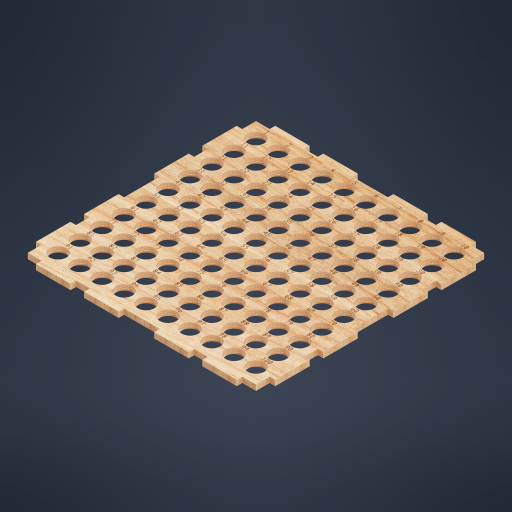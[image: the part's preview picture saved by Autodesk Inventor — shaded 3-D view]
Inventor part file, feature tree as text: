
AUTODESK INVENTOR PART (.ipt)
format: ipt  version: 2024.1 (Build 281209000, 209)  size: 6,590,464 bytes
history: native  units: mm
features: extrude x2, sketch x2, projected_geometry x1
ambient origin geometry x8: Origin, YZ Plane, XZ Plane, XY Plane, X Axis, Y Axis, Z Axis, Center Point
bodies: Solid1 (feature_tree)
feature tree (5):
  extrude  "Extrusion1"  Depth=100.0mm
  extrude  "Extrusion2"  Depth=5.0mm
  sketch  "Sketch1"  dims[d0=12.0mm d1=100.0mm d3=16.0mm]
  sketch  "Sketch2"  dims[d4=100.0mm d6=16.0mm d9=5.0mm d10=5.0mm d11=4.0mm d12=4.0mm d13=10.0mm d14=10.0mm d15=25.0mm d16=4.0mm d17=25.0mm d18=10.0mm d19=25.0mm d20=10.0mm d21=25.0mm d22=4.0mm d23=40.0mm d25=360.0deg d27=4.0mm d28=0.0mm d29=3.0mm d30=0.5mm d31=16.0mm d32=4.0mm d33=3.0mm d34=4.0mm d35=3.0mm d36=4.0mm d37=3.0mm d38=4.0mm d39=3.0mm d40=4.0mm d41=3.0mm d42=4.0mm d43=3.0mm d44=4.0mm d45=3.0mm d46=4.0mm d47=3.0mm d48=4.0mm d49=3.0mm d50=4.0mm d51=3.0mm d52=4.0mm d53=3.0mm d54=4.0mm d55=3.0mm d56=4.0mm d57=3.0mm d58=4.0mm d59=3.0mm d60=4.0mm d61=3.0mm d62=4.0mm d63=3.0mm d64=4.0mm d65=3.0mm d66=4.0mm d67=3.0mm d68=4.0mm d69=3.0mm d70=4.0mm d71=3.0mm d72=4.0mm d73=3.0mm d74=4.0mm d75=3.0mm d76=4.0mm d77=3.0mm d78=4.0mm d79=3.0mm d80=4.0mm d81=3.0mm d82=4.0mm d83=3.0mm d84=4.0mm d85=3.0mm d86=4.0mm d87=3.0mm d88=4.0mm d89=3.0mm d90=4.0mm d91=3.0mm d92=4.0mm d93=3.0mm d94=4.0mm d95=3.0mm d96=4.0mm d97=3.0mm d98=4.0mm d99=3.0mm d100=4.0mm d101=3.0mm d102=4.0mm d103=3.0mm d104=4.0mm d105=3.0mm d106=4.0mm d107=3.0mm d108=4.0mm d109=3.0mm d110=4.0mm d111=3.0mm d112=4.0mm d113=3.0mm d114=4.0mm d115=3.0mm d116=4.0mm d117=3.0mm d118=4.0mm d119=3.0mm d120=4.0mm d121=3.0mm d122=4.0mm d123=3.0mm d124=4.0mm d125=3.0mm d126=4.0mm d127=3.0mm d128=4.0mm d129=3.0mm d130=4.0mm d131=3.0mm d132=4.0mm d133=3.0mm d134=4.0mm d135=3.0mm d136=4.0mm d137=3.0mm d138=4.0mm d139=3.0mm d140=4.0mm d141=3.0mm d142=4.0mm d143=3.0mm d144=4.0mm d145=3.0mm d146=4.0mm d147=3.0mm d148=4.0mm d149=3.0mm d150=4.0mm d151=3.0mm d152=4.0mm d153=3.0mm d154=4.0mm d155=3.0mm d156=4.0mm d157=3.0mm d158=4.0mm d159=3.0mm d160=4.0mm d161=3.0mm d162=4.0mm d163=3.0mm d164=4.0mm d165=3.0mm d166=4.0mm d167=3.0mm d168=4.0mm d169=3.0mm d170=4.0mm d171=3.0mm d172=4.0mm d173=3.0mm d174=4.0mm d175=3.0mm d176=4.0mm d177=3.0mm d178=4.0mm d179=3.0mm d180=4.0mm d181=3.0mm d182=4.0mm d183=3.0mm d184=4.0mm d185=3.0mm d186=4.0mm d187=3.0mm d188=4.0mm d189=3.0mm d190=4.0mm d191=3.0mm d192=4.0mm d193=3.0mm d194=4.0mm d195=3.0mm d196=4.0mm d197=3.0mm d198=4.0mm d199=3.0mm d200=4.0mm d201=3.0mm d202=4.0mm d203=3.0mm d204=4.0mm d205=3.0mm d206=4.0mm d207=3.0mm d208=4.0mm d209=3.0mm d210=4.0mm d211=3.0mm d212=4.0mm d213=3.0mm d214=4.0mm d215=3.0mm d216=4.0mm d217=3.0mm d218=4.0mm d219=3.0mm d220=4.0mm d221=3.0mm d222=4.0mm d223=3.0mm d224=4.0mm d225=3.0mm d226=4.0mm d227=3.0mm d228=4.0mm d229=3.0mm d230=4.0mm d231=0.5mm d232=0.5mm d233=0.5mm d234=0.5mm d235=0.5mm d236=0.5mm d237=0.5mm d238=0.5mm d239=0.5mm d240=1.0mm d241=0.0mm]
  projected_geometry  "Project Cut Edges1"
